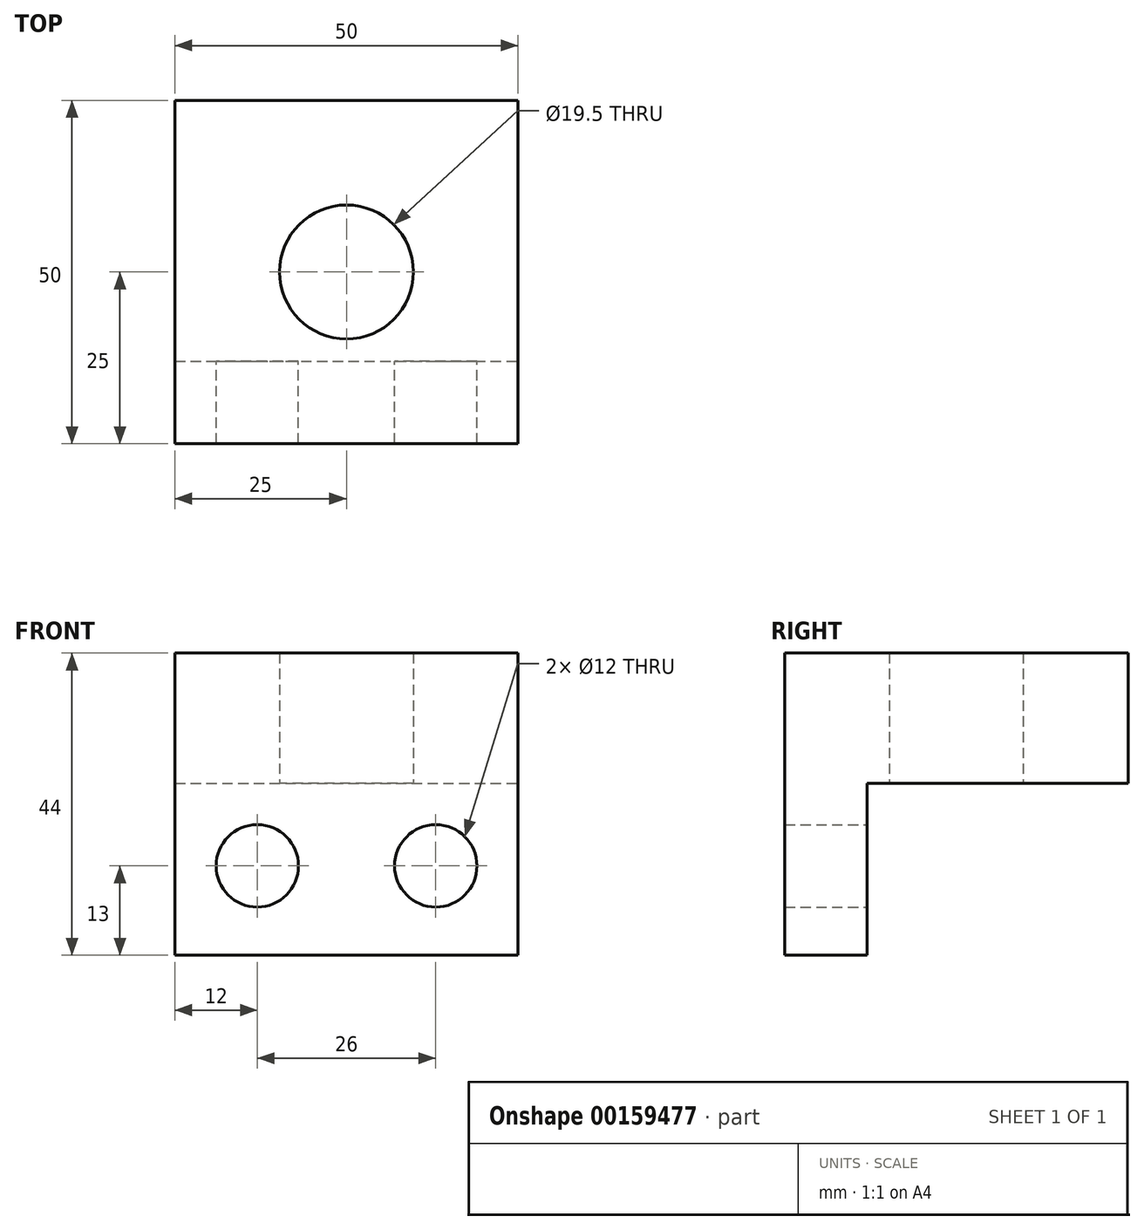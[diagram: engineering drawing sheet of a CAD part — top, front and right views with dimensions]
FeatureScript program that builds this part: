
annotation { "Feature Type Name" : "Feature", "Feature Type Description" : "" }
export const myFeature = defineFeature(function(context is Context, id is Id, definition is map)
    precondition{}
    {
        {
            var Q0;
            Q0=qCreatedBy(makeId("Top.planeOp"),FACE);
            var sketch = newSketch(context, id + "F0", { "sketchPlane" : qUnion([Q0])});
            skLineSegment(sketch, "E0.bottom", {"start": v(0, 0) * mm, "end": v(50, 0) * mm});
            skLineSegment(sketch, "E0.top", {"start": v(0, 50) * mm, "end": v(50, 50) * mm});
            skLineSegment(sketch, "E0.left", {"start": v(0, 0) * mm, "end": v(0, 50) * mm});
            skLineSegment(sketch, "E0.right", {"start": v(50, 0) * mm, "end": v(50, 50) * mm});
            skCircle(sketch, "E1", {"center": v(25, 25) * mm, "radius": 9.75 * mm});
            skSolve(sketch);
        }
        {
            var Q0;
            Q0 = qSketchRegion(id + "F0", true);
            extrude(context, id + "F1", {"entities" : qUnion([Q0]), "depth" : 19 * mm});
        }
        {
            var Q0;
            Q0=makeQuery(id+"F1.opExtrude","CAP_FACE",FACE,{"disambiguationData":[OSD([sQuery(id+"F0.wireOp",EDGE,"E0.bottom"),sQuery(id+"F0.wireOp",EDGE,"E0.top"),sQuery(id+"F0.wireOp",EDGE,"E0.left"),sQuery(id+"F0.wireOp",EDGE,"E0.right"),sQuery(id+"F0.wireOp",EDGE,"E1")])],"isStart":true});
            var sketch = newSketch(context, id + "F2", { "sketchPlane" : qUnion([Q0])});
            skLineSegment(sketch, "E2.bottom", {"start": v(0, 0) * mm, "end": v(50, 0) * mm});
            skLineSegment(sketch, "E2.top", {"start": v(0, -12) * mm, "end": v(50, -12) * mm});
            skLineSegment(sketch, "E2.left", {"start": v(0, 0) * mm, "end": v(0, -12) * mm});
            skLineSegment(sketch, "E2.right", {"start": v(50, 0) * mm, "end": v(50, -12) * mm});
            skSolve(sketch);
        }
        {
            var Q0;
            Q0 = qSketchRegion(id + "F2", true);
            extrude(context, id + "F3", {"entities" : qUnion([Q0]), "operationType" : NewBodyOperationType.ADD, "depth" : 25 * mm});
        }
        {
            var Q0;
            Q0=makeQuery(id+"F3.opExtrude","SWEPT_FACE",FACE,{"disambiguationData":[OSD([sQuery(id+"F2.wireOp",EDGE,"E2.top")])]});
            var sketch = newSketch(context, id + "F4", { "sketchPlane" : qUnion([Q0])});
            skCircle(sketch, "E3", {"center": v(-38, -12) * mm, "radius": 6 * mm});
            skCircle(sketch, "E4", {"center": v(-12, -12) * mm, "radius": 6 * mm});
            skSolve(sketch);
        }
        {
            var Q0;
            Q0 = qSketchRegion(id + "F4", true);
            extrude(context, id + "F5", {"entities" : qUnion([Q0]), "operationType" : NewBodyOperationType.REMOVE, "endBound" : BoundingType.THROUGH_ALL, "oppositeDirection" : true, "depth" : 25 * mm});
        }
    });
